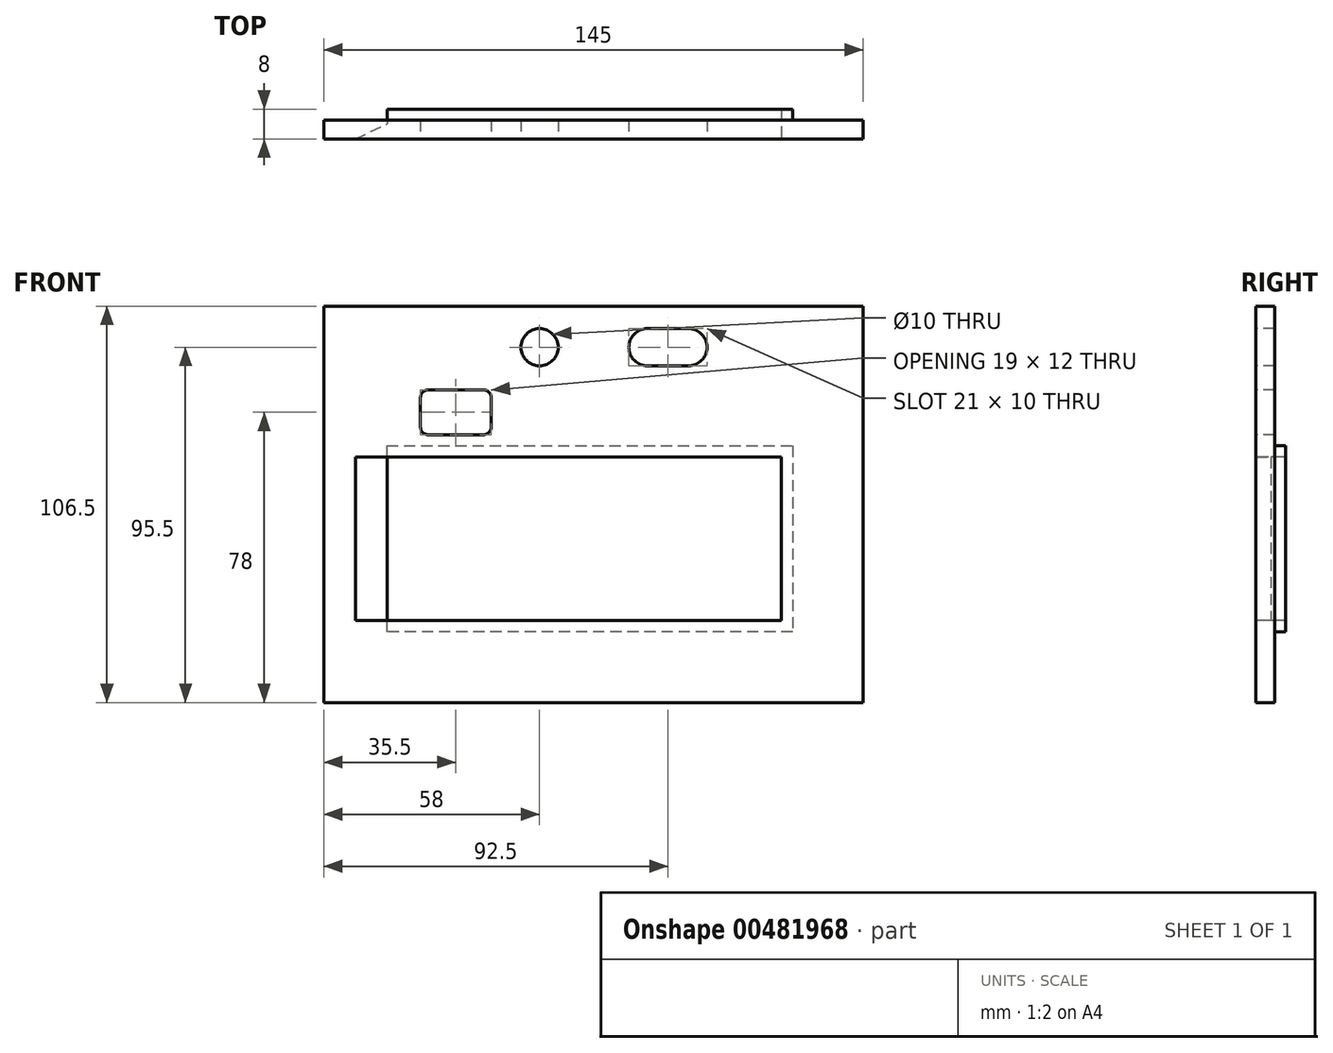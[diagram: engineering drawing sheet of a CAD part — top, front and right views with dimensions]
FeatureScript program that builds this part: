
annotation { "Feature Type Name" : "Feature", "Feature Type Description" : "" }
export const myFeature = defineFeature(function(context is Context, id is Id, definition is map)
    precondition{}
    {
        {
            var Q0;
            Q0=qCreatedBy(makeId("Front.planeOp"),FACE);
            var sketch = newSketch(context, id + "F0", { "sketchPlane" : qUnion([Q0])});
            skLineSegment(sketch, "E0.bottom", {"start": v(0, 0) * mm, "end": v(145, 0) * mm});
            skLineSegment(sketch, "E0.top", {"start": v(0, 106.5) * mm, "end": v(145, 106.5) * mm});
            skLineSegment(sketch, "E0.left", {"start": v(0, 0) * mm, "end": v(0, 106.5) * mm});
            skLineSegment(sketch, "E0.right", {"start": v(145, 0) * mm, "end": v(145, 106.5) * mm});
            skLineSegment(sketch, "E1.bottom", {"start": v(17, 66) * mm, "end": v(123, 66) * mm});
            skLineSegment(sketch, "E1.top", {"start": v(17, 22) * mm, "end": v(123, 22) * mm});
            skLineSegment(sketch, "E1.left", {"start": v(17, 66) * mm, "end": v(17, 22) * mm});
            skLineSegment(sketch, "E1.right", {"start": v(123, 66) * mm, "end": v(123, 22) * mm});
            skLineSegment(sketch, "E2", {"start": v(-30.97, 95.5) * mm, "end": v(199.57, 95.5) * mm, "construction": true});
            skCircle(sketch, "E3", {"center": v(58, 95.5) * mm, "radius": 5 * mm});
            skLineSegment(sketch, "E4.bottom", {"start": v(98, 100.5) * mm, "end": v(87, 100.5) * mm});
            skLineSegment(sketch, "E4.top", {"start": v(98, 90.5) * mm, "end": v(87, 90.5) * mm});
            skLineSegment(sketch, "E4.left", {"start": v(103, 95.5) * mm, "end": v(103, 95.5) * mm});
            skLineSegment(sketch, "E4.right", {"start": v(82, 95.5) * mm, "end": v(82, 95.5) * mm});
            skPoint(sketch, "E4.middle", {"position": v(92.5, 95.5) * mm});
            skPoint(sketch, "E5.visualSharp", {"position": v(82, 100.5) * mm});
            skArc(sketch, "E5.filletArc", {"start": v(87, 100.5) * mm, "mid": v(83.46, 99.04) * mm, "end": v(82, 95.5) * mm});
            skPoint(sketch, "E6.visualSharp", {"position": v(82, 90.5) * mm});
            skArc(sketch, "E6.filletArc", {"start": v(82, 95.5) * mm, "mid": v(83.46, 91.96) * mm, "end": v(87, 90.5) * mm});
            skPoint(sketch, "E7.visualSharp", {"position": v(103, 90.5) * mm});
            skArc(sketch, "E7.filletArc", {"start": v(98, 90.5) * mm, "mid": v(101.54, 91.96) * mm, "end": v(103, 95.5) * mm});
            skPoint(sketch, "E8.visualSharp", {"position": v(103, 100.5) * mm});
            skArc(sketch, "E8.filletArc", {"start": v(103, 95.5) * mm, "mid": v(101.54, 99.04) * mm, "end": v(98, 100.5) * mm});
            skLineSegment(sketch, "E9.bottom", {"start": v(28, 84) * mm, "end": v(43, 84) * mm});
            skLineSegment(sketch, "E9.top", {"start": v(28, 72) * mm, "end": v(43, 72) * mm});
            skLineSegment(sketch, "E9.left", {"start": v(26, 82) * mm, "end": v(26, 74) * mm});
            skLineSegment(sketch, "E9.right", {"start": v(45, 82) * mm, "end": v(45, 74) * mm});
            skPoint(sketch, "E10.visualSharp", {"position": v(26, 84) * mm});
            skArc(sketch, "E10.filletArc", {"start": v(28, 84) * mm, "mid": v(26.59, 83.41) * mm, "end": v(26, 82) * mm});
            skPoint(sketch, "E11.visualSharp", {"position": v(26, 72) * mm});
            skArc(sketch, "E11.filletArc", {"start": v(26, 74) * mm, "mid": v(26.59, 72.59) * mm, "end": v(28, 72) * mm});
            skPoint(sketch, "E12.visualSharp", {"position": v(45, 84) * mm});
            skArc(sketch, "E12.filletArc", {"start": v(45, 82) * mm, "mid": v(44.41, 83.41) * mm, "end": v(43, 84) * mm});
            skPoint(sketch, "E13.visualSharp", {"position": v(45, 72) * mm});
            skArc(sketch, "E13.filletArc", {"start": v(43, 72) * mm, "mid": v(44.41, 72.59) * mm, "end": v(45, 74) * mm});
            skSolve(sketch);
        }
        {
            var Q0;
            Q0=makeQuery(id+"F0.imprint","IMPRINT",FACE,{"disambiguationData":[TD([[makeQuery(id+"F0.imprint","IMPRINT",EDGE,{"derivedFrom":sQuery(id+"F0.wireOp",EDGE,"E0.bottom")}),1.0]])]});
            extrude(context, id + "F1", {"entities" : qUnion([Q0]), "oppositeDirection" : true, "depth" : 5 * mm});
        }
        {
            var Q0;
            Q0=makeQuery(id+"F1.opExtrude","CAP_EDGE",EDGE,{"disambiguationData":[OSD([sQuery(id+"F0.wireOp",EDGE,"E1.left")])],"isStart":true});
            chamfer(context, id + "F2", {"entities" : qUnion([Q0]), "chamferType" : ChamferType.TWO_OFFSETS, "width1" : 4 * mm, "oppositeDirection" : false, "width2" : 8.5 * mm, "tangentPropagation" : true});
        }
        {
            var Q0;
            Q0=makeQuery(id+"F1.opExtrude","CAP_FACE",FACE,{"disambiguationData":[OSD([sQuery(id+"F0.wireOp",EDGE,"E0.bottom"),sQuery(id+"F0.wireOp",EDGE,"E0.top"),sQuery(id+"F0.wireOp",EDGE,"E0.left"),sQuery(id+"F0.wireOp",EDGE,"E0.right"),sQuery(id+"F0.wireOp",EDGE,"E1.bottom"),sQuery(id+"F0.wireOp",EDGE,"E1.top"),sQuery(id+"F0.wireOp",EDGE,"E1.left"),sQuery(id+"F0.wireOp",EDGE,"E1.right"),sQuery(id+"F0.wireOp",EDGE,"E3"),sQuery(id+"F0.wireOp",EDGE,"E4.bottom"),sQuery(id+"F0.wireOp",EDGE,"E4.top"),sQuery(id+"F0.wireOp",EDGE,"E5.filletArc"),sQuery(id+"F0.wireOp",EDGE,"E6.filletArc"),sQuery(id+"F0.wireOp",EDGE,"E7.filletArc"),sQuery(id+"F0.wireOp",EDGE,"E8.filletArc"),sQuery(id+"F0.wireOp",EDGE,"E9.bottom"),sQuery(id+"F0.wireOp",EDGE,"E9.top"),sQuery(id+"F0.wireOp",EDGE,"E9.left"),sQuery(id+"F0.wireOp",EDGE,"E9.right"),sQuery(id+"F0.wireOp",EDGE,"E10.filletArc"),sQuery(id+"F0.wireOp",EDGE,"E11.filletArc"),sQuery(id+"F0.wireOp",EDGE,"E12.filletArc"),sQuery(id+"F0.wireOp",EDGE,"E13.filletArc")])],"isStart":false});
            var sketch = newSketch(context, id + "F3", { "sketchPlane" : qUnion([Q0])});
            skLineSegment(sketch, "E14", {"start": v(-17, 66) * mm, "end": v(-17, 69) * mm});
            skLineSegment(sketch, "E15", {"start": v(-17, 69) * mm, "end": v(-126, 69) * mm});
            skLineSegment(sketch, "E16", {"start": v(-126, 69) * mm, "end": v(-126, 19) * mm});
            skLineSegment(sketch, "E17", {"start": v(-126, 19) * mm, "end": v(-17, 19) * mm});
            skLineSegment(sketch, "E18", {"start": v(-17, 19) * mm, "end": v(-17, 22) * mm});
            skLineSegment(sketch, "E19", {"start": v(-17, 22) * mm, "end": v(-123, 22) * mm});
            skLineSegment(sketch, "E20", {"start": v(-123, 22) * mm, "end": v(-123, 66) * mm});
            skLineSegment(sketch, "E21", {"start": v(-123, 66) * mm, "end": v(-17, 66) * mm});
            skSolve(sketch);
        }
        {
            var Q0;
            Q0=makeQuery(id+"F3.imprint","IMPRINT",FACE,{"disambiguationData":[TD([[makeQuery(id+"F3.imprint","IMPRINT",EDGE,{"derivedFrom":sQuery(id+"F3.wireOp",EDGE,"E14")}),1.0]])]});
            extrude(context, id + "F4", {"entities" : qUnion([Q0]), "operationType" : NewBodyOperationType.ADD, "depth" : 3 * mm});
        }
    });
